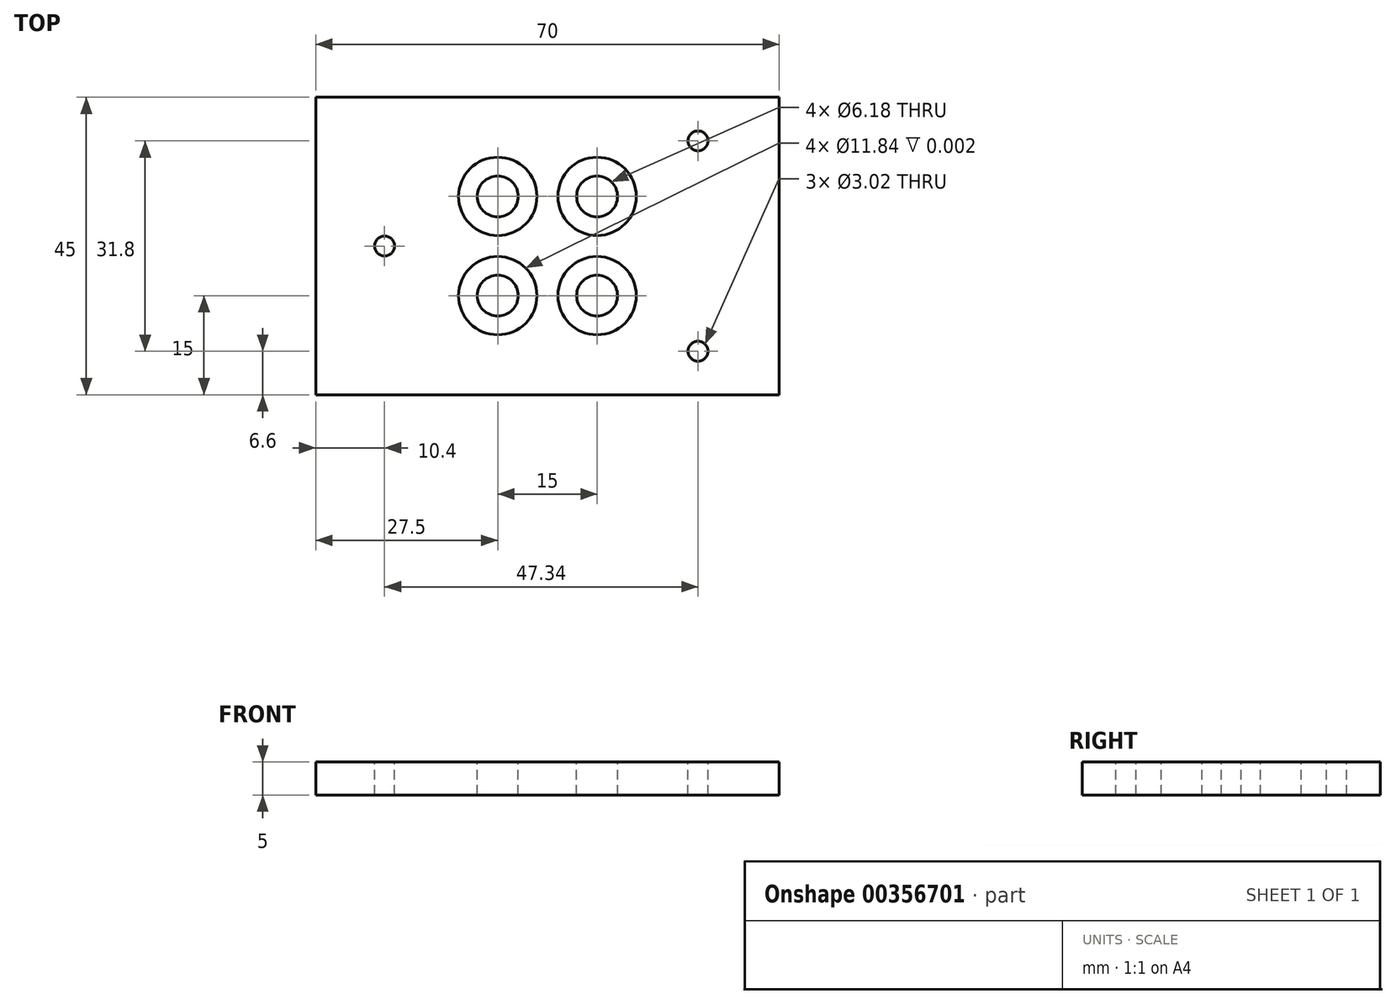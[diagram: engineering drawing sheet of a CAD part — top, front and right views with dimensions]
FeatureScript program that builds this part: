
annotation { "Feature Type Name" : "Feature", "Feature Type Description" : "" }
export const myFeature = defineFeature(function(context is Context, id is Id, definition is map)
    precondition{}
    {
        {
            var Q0;
            Q0=qCreatedBy(makeId("Top.planeOp"),FACE);
            var sketch = newSketch(context, id + "F0", { "sketchPlane" : qUnion([Q0])});
            skLineSegment(sketch, "E0", {"start": v(-34.2, -20) * mm, "end": v(-34.2, 11.8) * mm, "construction": true});
            skLineSegment(sketch, "E1", {"start": v(-34.2, 11.79) * mm, "end": v(-32.8, 11.79) * mm, "construction": true});
            skLineSegment(sketch, "E2", {"start": v(-32.8, 11.8) * mm, "end": v(-32.8, 20) * mm, "construction": true});
            skLineSegment(sketch, "E3", {"start": v(-32.8, 20) * mm, "end": v(21.8, 20) * mm, "construction": true});
            skLineSegment(sketch, "E4", {"start": v(21.8, 20) * mm, "end": v(32.8, 9.1) * mm, "construction": true});
            skLineSegment(sketch, "E5", {"start": v(32.8, 9.1) * mm, "end": v(32.8, -9.1) * mm, "construction": true});
            skLineSegment(sketch, "E6", {"start": v(32.8, -9.1) * mm, "end": v(21.8, -20) * mm, "construction": true});
            skLineSegment(sketch, "E7", {"start": v(-34.2, -20) * mm, "end": v(21.8, -20) * mm, "construction": true});
            skCircle(sketch, "E8", {"center": v(-25.3, 0) * mm, "radius": 1 * mm});
            skCircle(sketch, "E9", {"center": v(22.04, 15.9) * mm, "radius": 1 * mm});
            skCircle(sketch, "E10", {"center": v(22.04, -15.9) * mm, "radius": 1 * mm});
            skSolve(sketch);
        }
        {
            var Q0;
            Q0=qCreatedBy(makeId("Top.planeOp"),FACE);
            var sketch = newSketch(context, id + "F1", { "sketchPlane" : qUnion([Q0])});
            skLineSegment(sketch, "E11.bottom", {"start": v(-35.7, 22.5) * mm, "end": v(34.3, 22.5) * mm});
            skLineSegment(sketch, "E11.top", {"start": v(-35.7, -22.5) * mm, "end": v(34.3, -22.5) * mm});
            skLineSegment(sketch, "E11.left", {"start": v(-35.7, 22.5) * mm, "end": v(-35.7, -22.5) * mm});
            skLineSegment(sketch, "E11.right", {"start": v(34.3, 22.5) * mm, "end": v(34.3, -22.5) * mm});
            skSolve(sketch);
        }
        {
            var Q0;
            Q0=makeQuery(id+"F1.imprint","IMPRINT",FACE,{"disambiguationData":[TD([[makeQuery(id+"F1.imprint","IMPRINT",EDGE,{"derivedFrom":sQuery(id+"F1.wireOp",EDGE,"E11.bottom")}),-1.0]])]});
            extrude(context, id + "F2", {"entities" : qUnion([Q0]), "oppositeDirection" : true, "depth" : 5 * mm});
        }
        {
            var Q0;
            Q0=qCreatedBy(makeId("Top.planeOp"),FACE);
            var sketch = newSketch(context, id + "F3", { "sketchPlane" : qUnion([Q0])});
            skCircle(sketch, "E12.0", {"center": v(-25.3, 0) * mm, "radius": 1 * mm, "construction": true});
            skCircle(sketch, "E13.0", {"center": v(22.04, 15.9) * mm, "radius": 1 * mm, "construction": true});
            skCircle(sketch, "E14.0", {"center": v(22.04, -15.9) * mm, "radius": 1 * mm, "construction": true});
            skCircle(sketch, "E15", {"center": v(-25.3, 0) * mm, "radius": 1.5 * mm});
            skCircle(sketch, "E16", {"center": v(22.04, 15.9) * mm, "radius": 1.5 * mm});
            skCircle(sketch, "E17", {"center": v(22.04, -15.9) * mm, "radius": 1.5 * mm});
            skSolve(sketch);
        }
        {
            var Q0;
            Q0=qSketchRegion(id+"F3",true);
            extrude(context, id + "F4", {"entities" : qUnion([Q0]), "operationType" : NewBodyOperationType.REMOVE, "oppositeDirection" : true, "depth" : 25 * mm});
        }
        {
            var Q0;
            Q0=qCreatedBy(makeId("Top.planeOp"),FACE);
            var sketch = newSketch(context, id + "F5", { "sketchPlane" : qUnion([Q0])});
            skLineSegment(sketch, "E18.bottom", {"start": v(-8.2, 7.5) * mm, "end": v(6.8, 7.5) * mm, "construction": true});
            skLineSegment(sketch, "E18.top", {"start": v(-8.2, -7.5) * mm, "end": v(6.8, -7.5) * mm, "construction": true});
            skLineSegment(sketch, "E18.left", {"start": v(-8.2, 7.5) * mm, "end": v(-8.2, -7.5) * mm, "construction": true});
            skLineSegment(sketch, "E18.right", {"start": v(6.8, 7.5) * mm, "end": v(6.8, -7.5) * mm, "construction": true});
            skLineSegment(sketch, "E19", {"start": v(-51.67, 0) * mm, "end": v(66.42, 0) * mm, "construction": true});
            skLineSegment(sketch, "E20", {"start": v(-0.7, 32.47) * mm, "end": v(-0.7, -44.14) * mm, "construction": true});
            skCircle(sketch, "E21", {"center": v(-8.2, 7.5) * mm, "radius": 3.09 * mm});
            skCircle(sketch, "E22", {"center": v(6.8, 7.5) * mm, "radius": 3.09 * mm});
            skCircle(sketch, "E23", {"center": v(-8.2, -7.5) * mm, "radius": 3.09 * mm});
            skCircle(sketch, "E24", {"center": v(6.8, -7.5) * mm, "radius": 3.09 * mm});
            skSolve(sketch);
        }
        {
            var Q0;
            Q0=qSketchRegion(id+"F5",true);
            extrude(context, id + "F6", {"entities" : qUnion([Q0]), "operationType" : NewBodyOperationType.REMOVE, "oppositeDirection" : true, "depth" : 25 * mm});
        }
        {
            var Q0;
            Q0=makeQuery(id+"F2.opExtrude","CAP_FACE",FACE,{"disambiguationData":[OSD([sQuery(id+"F1.wireOp",EDGE,"E11.bottom"),sQuery(id+"F1.wireOp",EDGE,"E11.top"),sQuery(id+"F1.wireOp",EDGE,"E11.left"),sQuery(id+"F1.wireOp",EDGE,"E11.right")])],"isStart":true});
            var sketch = newSketch(context, id + "F7", { "sketchPlane" : qUnion([Q0])});
            skCircle(sketch, "E25", {"center": v(-8.2, 7.5) * mm, "radius": 5.92 * mm});
            skCircle(sketch, "E26", {"center": v(6.8, 7.5) * mm, "radius": 5.92 * mm});
            skCircle(sketch, "E27", {"center": v(-8.2, -7.5) * mm, "radius": 5.92 * mm});
            skCircle(sketch, "E28", {"center": v(6.8, -7.5) * mm, "radius": 5.92 * mm});
            skSolve(sketch);
        }
        {
            var Q0;
            Q0=qSketchRegion(id+"F7",true);
            extrude(context, id + "F8", {"entities" : qUnion([Q0]), "operationType" : NewBodyOperationType.REMOVE, "oppositeDirection" : true, "depth" : 1 / 406.4 * mm});
        }
    });
